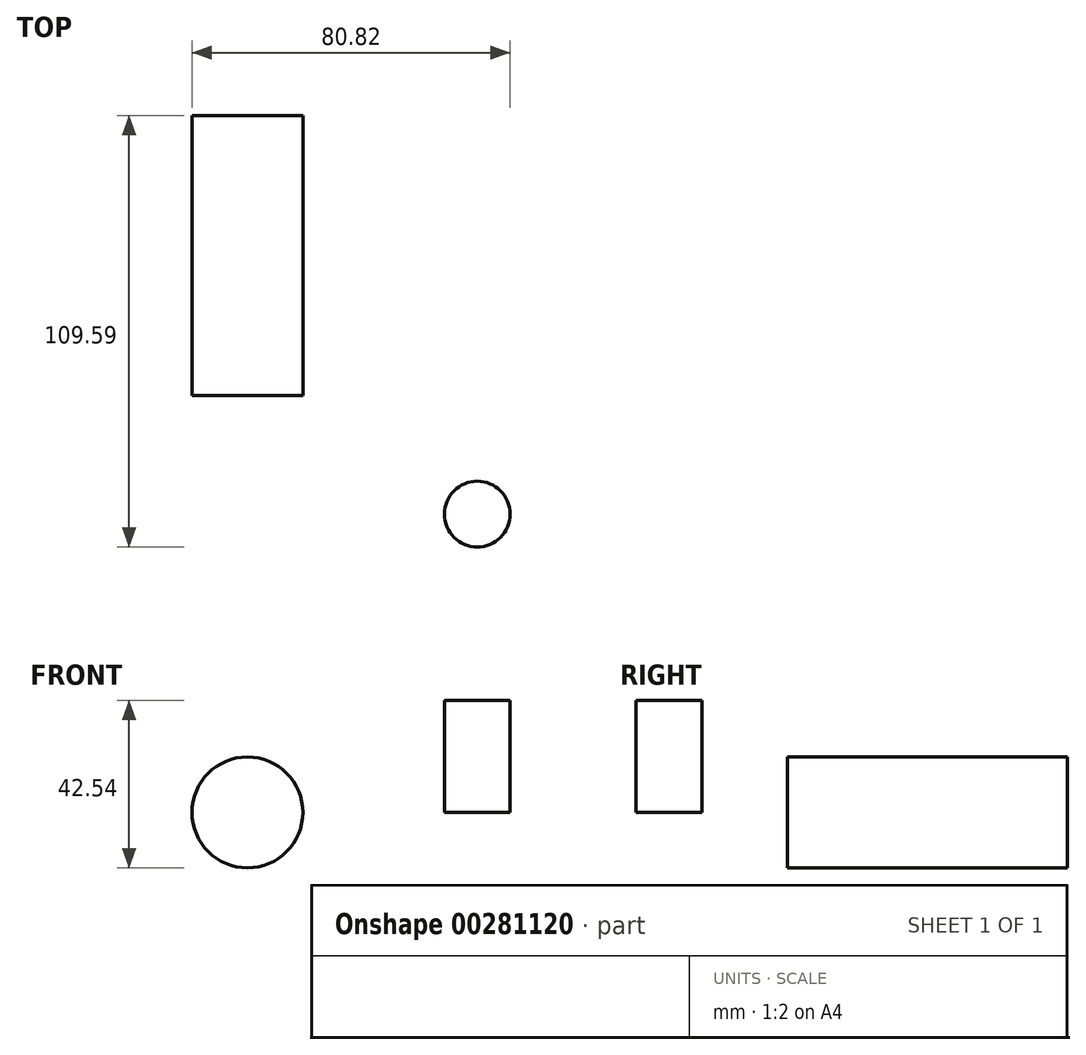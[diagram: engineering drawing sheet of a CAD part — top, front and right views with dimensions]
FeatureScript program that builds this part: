
annotation { "Feature Type Name" : "Feature", "Feature Type Description" : "" }
export const myFeature = defineFeature(function(context is Context, id is Id, definition is map)
    precondition{}
    {
        {
            var Q0;
            Q0=qCreatedBy(makeId("Front.planeOp"),FACE);
            var sketch = newSketch(context, id + "F0", { "sketchPlane" : qUnion([Q0])});
            skLineSegment(sketch, "E0.bottom", {"start": v(-33.31, -33.16) * mm, "end": v(33.31, -33.16) * mm});
            skLineSegment(sketch, "E0.top", {"start": v(-33.31, 33.16) * mm, "end": v(33.31, 33.16) * mm});
            skLineSegment(sketch, "E0.left", {"start": v(-33.31, -33.16) * mm, "end": v(-33.31, 33.16) * mm});
            skLineSegment(sketch, "E0.right", {"start": v(33.31, -33.16) * mm, "end": v(33.31, 33.16) * mm});
            skPoint(sketch, "E0.middle", {"position": v(0, 0) * mm});
            skCircle(sketch, "E1", {"center": v(0, 0) * mm, "radius": 14.09 * mm});
            skSolve(sketch);
        }
        {
            var Q0;
            Q0=qCreatedBy(makeId("Right.planeOp"),FACE);
            cPlane(context, id + "F1", {"entities" : qUnion([Q0]), "cplaneType" : CPlaneType.OFFSET, "offset" : 33.31 * mm, "oppositeDirection" : true, "width" : 152.4 * mm, "height" : 152.4 * mm});
        }
        {
            var Q0;
            Q0=qCreatedBy(makeId("Right.planeOp"),FACE);
            cPlane(context, id + "F2", {"entities" : qUnion([Q0]), "cplaneType" : CPlaneType.OFFSET, "offset" : 33.31 * mm, "width" : 152.4 * mm, "height" : 152.4 * mm});
        }
        {
            var Q0;
            Q0=sQuery(id+"F0.wireOp",EDGE,"E1");
            extrude(context, id + "F3", {"bodyType" : ToolBodyType.SURFACE, "surfaceEntities" : qUnion([Q0]), "endBound" : BoundingType.SYMMETRIC, "depth" : 71.12 * mm});
        }
        {
            var Q0;
            Q0=qCreatedBy(makeId("Top.planeOp"),FACE);
            var sketch = newSketch(context, id + "F4", { "sketchPlane" : qUnion([Q0])});
            skCircle(sketch, "E2", {"center": v(58.37, -65.68) * mm, "radius": 8.36 * mm});
            skSolve(sketch);
        }
        {
            var Q0;
            Q0=sQuery(id+"F4.wireOp",EDGE,"E2");
            extrude(context, id + "F5", {"bodyType" : ToolBodyType.SURFACE, "surfaceEntities" : qUnion([Q0]), "depth" : 28.45 * mm});
        }
    });
